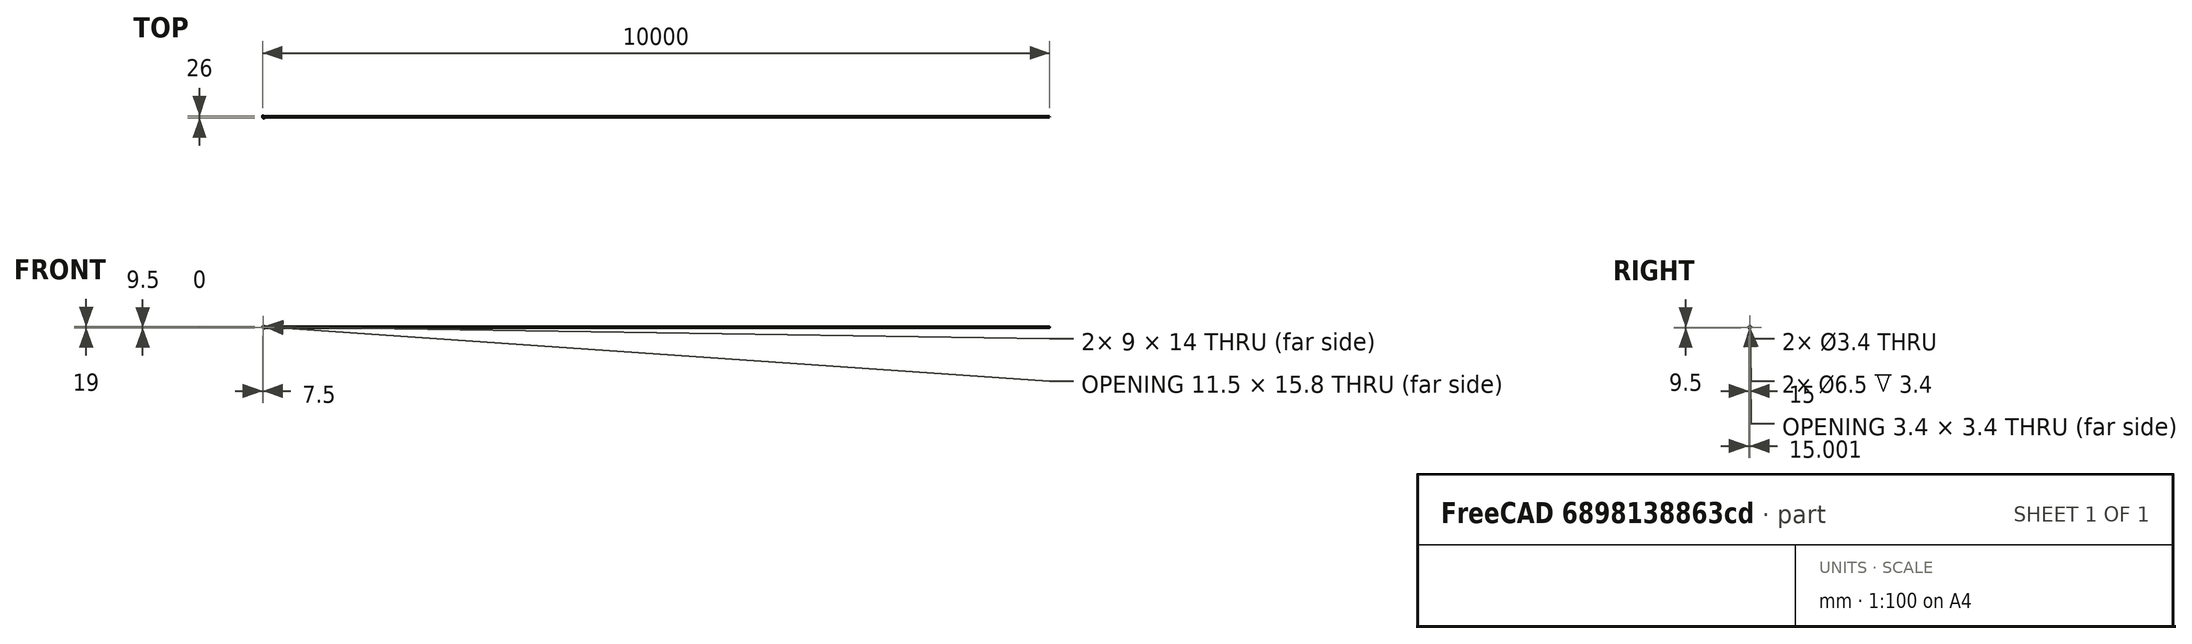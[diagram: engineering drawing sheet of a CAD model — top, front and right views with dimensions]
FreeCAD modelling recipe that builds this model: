
FCSTD DOCUMENT  (FreeCAD 0.14R3702 (Git))
Label: extruder-air-nozzle
License: CC-BY 3.0
LicenseURL: http://creativecommons.org/licenses/by/3.0/
objects: Part::Feature×7, Sketcher::SketchObject×7, PartDesign::Pad×4, PartDesign::Pocket×3, Part::MultiFuse×3, Part::Cylinder×2, Mesh::Feature×1, Part::Cut×1
note: 34 computed .brp shape members not serialized (recipe doc carries the construction recipe); baked Part::Feature solids carry a one-line shape summary decoded from their .brp

FEATURE [Mesh::Feature] Tobera_05
FEATURE [Part::Feature] Tobera_05001
  shape: bbox 25 x 26 x 19 mm, 3312 faces, 0 solids (baked)
FEATURE [Part::Feature] Tobera_05001_solid  label="Tobera_05001 (Solid)"
  shape: bbox 25 x 26 x 19 mm, 3312 faces (baked)
FEATURE [Part::Feature] Tobera_05001_solid001  label="Tobera_05001 (Solid)001"
  shape: bbox 25 x 26 x 19 mm, 2032 faces (baked)
FEATURE [Part::Feature] Tobera_05001_solid_cs
  shape: bbox 25 x 26 x 2e-07 mm, 0 faces, 0 solids (baked)
FEATURE [Sketcher::SketchObject] Sketch  label="main-body-sketch"
  sketch-geometry (10):
    g0: LineSegment StartX=0 StartY=0 StartZ=0 EndX=-15 EndY=0 EndZ=0
    g1: LineSegment StartX=-15 StartY=0 StartZ=0 EndX=-15 EndY=-8 EndZ=0
    g2: LineSegment StartX=-2 StartY=-21 StartZ=0 EndX=3.42 EndY=-21 EndZ=0
    g3: ArcOfCircle CenterX=-2 CenterY=-8 CenterZ=0 NormalX=0 NormalY=0 NormalZ=1 Radius=13 StartAngle=3.14159 EndAngle=4.71239
    g4: LineSegment StartX=0 StartY=0 StartZ=0 EndX=0 EndY=-10 EndZ=0
    g5: LineSegment StartX=1.99785 StartY=-13.4896 StartZ=0 EndX=9.99785 EndY=-18.6059 EndZ=0
    g6: LineSegment StartX=3.42 StartY=-21 StartZ=0 EndX=9.99785 EndY=-18.6059 EndZ=0
    g7: LineSegment [constr] StartX=3.42 StartY=-21 StartZ=0 EndX=9.42 EndY=-21 EndZ=0
    g8: LineSegment [constr] StartX=9.99785 StartY=-18.6059 StartZ=0 EndX=3.99785 EndY=-18.6059 EndZ=0
    g9: ArcOfCircle CenterX=4.04659 CenterY=-10 CenterZ=0 NormalX=0 NormalY=0 NormalZ=1 Radius=4.04659 StartAngle=3.14159 EndAngle=4.18151
  constraints (31):
    c: Coincident(g0,g1)
    c: Horizontal(g0)
    c: Vertical(g1)
    c: Horizontal(g2)
    c: Coincident(g0,g-1)
    c: DistanceX(g0) = -15
    c: DistanceY(g1) = -8
    c: DistanceX(g2) = 5.42
    c: DistanceY(g-1,g2) = -21
    c: Coincident(g3,g2)
    c: Coincident(g3,g1)
    c: Tangent(g1,g3)
    c: Tangent(g2,g3)
    c: Coincident(g4,g-1)
    c: Vertical(g4)
    c: DistanceY(g4) = -10
    c: Coincident(g6,g2)
    c: Distance(g6) = 7
    c: Horizontal(g7)
    c: Coincident(g7,g2)
    c: DistanceX(g7) = 6
    c: Angle(g7,g6) = 0.349066
    c: Coincident(g5,g6)
    c: Horizontal(g8)
    c: Coincident(g8,g5)
    c: Angle(g5,g8) = 0.568977
    c: DistanceX(g8) = -6
    c: DistanceX(g5,g5) = -8
    c: Coincident(g9,g4)
    c: Coincident(g9,g5)
    c: Tangent(g4,g9)
FEATURE [PartDesign::Pad] Pad  label="main-body"
  Length = 19
  Length2 = 100
  Midplane = true
  Sketch = -> Sketch
  Type = 0
FEATURE [Sketcher::SketchObject] Sketch001  label="Inner-room-sketch"
  sketch-geometry (18):
    g0: LineSegment [constr] StartX=-12 StartY=0 StartZ=0 EndX=-3 EndY=0 EndZ=0
    g1: LineSegment StartX=-12 StartY=0 StartZ=0 EndX=-12 EndY=-7.3 EndZ=0
    g2: LineSegment StartX=-5.40703 StartY=-16.2671 StartZ=0 EndX=6.32941 EndY=-19.9338 EndZ=0
    g3: LineSegment StartX=-3 StartY=0 StartZ=0 EndX=-3 EndY=-6 EndZ=0
    g4: ArcOfCircle CenterX=7 CenterY=-6.00002 CenterZ=0 NormalX=0 NormalY=0 NormalZ=1 Radius=10 StartAngle=3.14159 EndAngle=4.14341
    g5: LineSegment StartX=1.61229 StartY=-14.4245 StartZ=0 EndX=8.81324 EndY=-19.0297 EndZ=0
    g6: LineSegment [constr] StartX=6.32941 StartY=-19.9338 StartZ=0 EndX=8.81324 EndY=-19.0297 EndZ=0
    g7: LineSegment [constr] StartX=6.32941 StartY=-19.9338 StartZ=0 EndX=0.329406 EndY=-19.9338 EndZ=0
    g8: LineSegment [constr] StartX=6.32941 StartY=-19.9338 StartZ=0 EndX=9.32941 EndY=-19.9338 EndZ=0
    g9: GeomPoint [constr] X=3.4 Y=-21 Z=0
    g10: LineSegment [constr] StartX=8.81324 StartY=-19.0297 StartZ=0 EndX=6.81324 EndY=-19.0297 EndZ=0
    g11: ArcOfCircle CenterX=-2.60553 CenterY=-7.30002 CenterZ=0 NormalX=0 NormalY=0 NormalZ=1 Radius=9.39447 StartAngle=3.14159 EndAngle=4.40957
    g12: LineSegment StartX=6.32941 StartY=-19.9338 StartZ=0 EndX=7.57927 EndY=-20.3243 EndZ=0
    g13: LineSegment StartX=7.57927 StartY=-20.3243 StartZ=0 EndX=9.65569 EndY=-19.5685 EndZ=0
    g14: LineSegment StartX=9.65569 StartY=-19.5685 StartZ=0 EndX=8.81324 EndY=-19.0297 EndZ=0
    g15: LineSegment StartX=-12 StartY=0 StartZ=0 EndX=-12 EndY=1 EndZ=0
    g16: LineSegment StartX=-12 StartY=1 StartZ=0 EndX=-3 EndY=1 EndZ=0
    g17: LineSegment StartX=-3 StartY=1 StartZ=0 EndX=-3 EndY=0 EndZ=0
  constraints (53):
    c: Horizontal(g0)
    c: PointOnObject(g0,g-1)
    c: DistanceX(g0) = 9
    c: DistanceX(g-1,g0) = -3
    c: Vertical(g1)
    c: Coincident(g1,g0)
    c: Coincident(g3,g0)
    c: Vertical(g3)
    c: DistanceY(g3) = -6
    c: Coincident(g4,g3)
    c: Tangent(g3,g4)
    c: Coincident(g6,g2)
    c: Horizontal(g7)
    c: Coincident(g7,g2)
    c: DistanceX(g7) = -6
    c: Angle(g2,g7) = 0.302815
    c: Horizontal(g8)
    c: Coincident(g8,g2)
    c: DistanceX(g8) = 3
    c: Angle(g8,g6) = 0.349066
    c: DistanceY(g-1,g9) = -21
    c: PointOnObject(g9,g6)
    c: Coincident(g5,g6)
    c: Horizontal(g10)
    c: Coincident(g10,g5)
    c: DistanceX(g10) = -2
    c: Angle(g5,g10) = 0.568977
    c: Coincident(g5,g4)
    c: DistanceX(g-1,g9) = 3.4
    c: Tangent(g4,g5)
    c: Radius(g4) = 10
    c: Coincident(g11,g1)
    c: Coincident(g11,g2)
    c: Tangent(g2,g11)
    c: Tangent(g1,g11)
    c: Radius(g11) = 9.39447
    c: DistanceY(g1) = -7.3
    c: Coincident(g12,g13)
    c: Coincident(g13,g14)
    c: Coincident(g14,g5)
    c: PointOnObject(g13,g5)
    c: Coincident(g12,g2)
    c: PointOnObject(g12,g2)
    c: Parallel(g6,g13)
    c: Distance(g14) = 1
    c: Coincident(g15,g16)
    c: Coincident(g16,g17)
    c: Horizontal(g16)
    c: Vertical(g15)
    c: Vertical(g17)
    c: Coincident(g15,g0)
    c: Coincident(g17,g0)
    c: DistanceY(g15) = 1
FEATURE [PartDesign::Pad] Pad001  label="Inner-room"
  Length = 17
  Length2 = 100
  Midplane = true
  Sketch = -> Sketch001
  Type = 0
FEATURE [Sketcher::SketchObject] Sketch002  label="inner-cutout-1-sketch"
  ExternalGeometry = -> [Pad001]
  Placement = pos=(-3,-4e-12,0) rot=(0.57735,0.57735,0.57735;2.0944rad)
  Support = -> Pad001 [Face10]
  sketch-geometry (8):
    g0: LineSegment StartX=-5 StartY=8.5 StartZ=0 EndX=1 EndY=8.5 EndZ=0
    g1: LineSegment StartX=1 StartY=8.5 StartZ=0 EndX=1 EndY=7 EndZ=0
    g2: LineSegment StartX=1 StartY=7 StartZ=0 EndX=-5 EndY=7 EndZ=0
    g3: LineSegment StartX=-5 StartY=7 StartZ=0 EndX=-5 EndY=8.5 EndZ=0
    g4: LineSegment StartX=-5 StartY=-7 StartZ=0 EndX=1 EndY=-7 EndZ=0
    g5: LineSegment StartX=1 StartY=-7 StartZ=0 EndX=1 EndY=-8.5 EndZ=0
    g6: LineSegment StartX=1 StartY=-8.5 StartZ=0 EndX=-5 EndY=-8.5 EndZ=0
    g7: LineSegment StartX=-5 StartY=-8.5 StartZ=0 EndX=-5 EndY=-7 EndZ=0
  constraints (23):
    c: Coincident(g0,g1)
    c: Coincident(g1,g2)
    c: Coincident(g2,g3)
    c: Coincident(g3,g0)
    c: Horizontal(g0)
    c: Horizontal(g2)
    c: Vertical(g1)
    c: Vertical(g3)
    c: PointOnObject(g0,g-3)
    c: DistanceY(g3) = 1.5
    c: PointOnObject(g1,g-4)
    c: DistanceX(g2) = -6
    c: Coincident(g4,g5)
    c: Coincident(g5,g6)
    c: Coincident(g6,g7)
    c: Coincident(g7,g4)
    c: Horizontal(g4)
    c: Horizontal(g6)
    c: Vertical(g5)
    c: Vertical(g7)
    c: Symmetric(g5,g0,g-1)
    c: Symmetric(g4,g1,g-1)
    c: Symmetric(g4,g2,g-1)
FEATURE [PartDesign::Pocket] Pocket  label="inner-cutout-1"
  Length = 5
  Sketch = -> Sketch002
  Type = 1
FEATURE [Part::Cut] Cut  label="body-1"
  Base = -> Pad
  Tool = -> Pocket
FEATURE [Part::Cylinder] Cylinder  label="screw-tube-1"
  Angle = 360
  Height = 11
  Placement = pos=(-12.6,-6,0) rot=(0,1,0;1.5708rad)
  Radius = 2.7
FEATURE [Part::Cylinder] Cylinder001  label="screw-tube-2"
  Angle = 360
  Height = 3.4
  Placement = pos=(-13,-6,0) rot=(0,1,0;1.5708rad)
  Radius = 4.25
FEATURE [Part::MultiFuse] Fusion  label="screw-tube"
  Shapes = -> [Cylinder,Cylinder001]
FEATURE [Part::MultiFuse] Fusion001  label="body-2"
  Shapes = -> [Cut,Fusion]
FEATURE [Sketcher::SketchObject] Sketch003  label="bolt-cap-cutout-sketch-1"
  Placement = pos=(-15,0,0) rot=(0.57735,-0.57735,-0.57735;2.0944rad)
  Support = -> Fusion001 [Face5]
  sketch-geometry (1):
    g0: Circle CenterX=6 CenterY=0 CenterZ=0 NormalX=0 NormalY=0 NormalZ=1 Radius=3.25
  constraints (3):
    c: Radius(g0) = 3.25
    c: PointOnObject(g0,g-1)
    c: DistanceX(g-1,g0) = 6
FEATURE [PartDesign::Pocket] Pocket001  label="bolt-cap-cutout-sketch-002"
  Length = 3.4
  Sketch = -> Sketch003
  Type = 0
FEATURE [Sketcher::SketchObject] Sketch004  label="drill-sketch"
  Placement = pos=(-15,0,0) rot=(0.57735,-0.57735,-0.57735;2.0944rad)
  Support = -> Pocket001 [Face5]
  sketch-geometry (1):
    g0: Circle CenterX=6 CenterY=0 CenterZ=0 NormalX=0 NormalY=0 NormalZ=1 Radius=1.7
  constraints (3):
    c: Radius(g0) = 1.7
    c: PointOnObject(g0,g-1)
    c: DistanceX(g-1,g0) = 6
FEATURE [PartDesign::Pocket] Pocket002  label="drill"
  Length = 5
  Sketch = -> Sketch004
  Type = 1
FEATURE [Sketcher::SketchObject] Sketch005  label="top-sketch"
  ExternalGeometry = -> [Pocket002]
  Placement = pos=(0,0,0) rot=(0,0.707107,0.707107;3.14159rad)
  Support = -> Pocket002 [Face1]
  sketch-geometry (15):
    g0: LineSegment StartX=3 StartY=7 StartZ=0 EndX=12 EndY=7 EndZ=0
    g1: LineSegment StartX=12 StartY=7 StartZ=0 EndX=12 EndY=-7 EndZ=0
    g2: LineSegment StartX=12 StartY=-7 StartZ=0 EndX=3 EndY=-7 EndZ=0
    g3: LineSegment StartX=3 StartY=-7 StartZ=0 EndX=3 EndY=7 EndZ=0
    g4: ArcOfCircle CenterX=3.25 CenterY=6.4 CenterZ=0 NormalX=0 NormalY=0 NormalZ=1 Radius=1.5 StartAngle=1.5708 EndAngle=3.14159
    g5: LineSegment [constr] StartX=1.75 StartY=6.4 StartZ=0 EndX=3.25 EndY=6.4 EndZ=0
    g6: LineSegment [constr] StartX=3.25 StartY=7.9 StartZ=0 EndX=3.25 EndY=6.4 EndZ=0
    g7: LineSegment [constr] StartX=7.5 StartY=7 StartZ=0 EndX=7.5 EndY=-7 EndZ=0
    g8: LineSegment StartX=3.25 StartY=7.9 StartZ=0 EndX=11.75 EndY=7.9 EndZ=0
    g9: LineSegment StartX=3.25 StartY=-7.9 StartZ=0 EndX=11.75 EndY=-7.9 EndZ=0
    g10: LineSegment StartX=1.75 StartY=6.4 StartZ=0 EndX=1.75 EndY=-6.4 EndZ=0
    g11: LineSegment StartX=13.25 StartY=6.4 StartZ=0 EndX=13.25 EndY=-6.4 EndZ=0
    g12: ArcOfCircle CenterX=11.75 CenterY=6.4 CenterZ=0 NormalX=0 NormalY=0 NormalZ=1 Radius=1.5 StartAngle=0 EndAngle=1.5708
    g13: ArcOfCircle CenterX=11.75 CenterY=-6.4 CenterZ=0 NormalX=0 NormalY=0 NormalZ=1 Radius=1.5 StartAngle=4.71239 EndAngle=6.28319
    g14: ArcOfCircle CenterX=3.25 CenterY=-6.4 CenterZ=0 NormalX=0 NormalY=0 NormalZ=1 Radius=1.5 StartAngle=3.14159 EndAngle=4.71239
  constraints (42):
    c: Coincident(g0,g1)
    c: Coincident(g1,g2)
    c: Coincident(g2,g3)
    c: Coincident(g3,g0)
    c: Horizontal(g2)
    c: Vertical(g1)
    c: Vertical(g3)
    c: Coincident(g0,g-3)
    c: Coincident(g-3,g0)
    c: Symmetric(g0,g2,g-1)
    c: Horizontal(g5)
    c: Coincident(g5,g4)
    c: Coincident(g4,g5)
    c: Radius(g4) = 1.5
    c: Vertical(g6)
    c: Coincident(g6,g4)
    c: Coincident(g4,g6)
    c: DistanceX(g4,g0) = 1.25
    c: DistanceY(g0,g4) = 0.9
    c: Symmetric(g7,g7,g-1)
    c: PointOnObject(g7,g0)
    c: Symmetric(g0,g0,g7)
    c: Horizontal(g8)
    c: Coincident(g8,g4)
    c: Symmetric(g4,g8,g7)
    c: Horizontal(g9)
    c: Symmetric(g4,g9,g-1)
    c: Symmetric(g9,g9,g7)
    c: Symmetric(g10,g10,g-1)
    c: Coincident(g10,g4)
    c: Vertical(g11)
    c: Symmetric(g11,g11,g-1)
    c: Symmetric(g11,g4,g7)
    c: Coincident(g12,g8)
    c: Coincident(g12,g11)
    c: Equal(g12,g4)
    c: Coincident(g13,g11)
    c: Coincident(g13,g9)
    c: Equal(g13,g12)
    c: Coincident(g14,g9)
    c: Coincident(g14,g10)
    c: Equal(g14,g13)
FEATURE [PartDesign::Pad] Pad002  label="top"
  Length = 5
  Length2 = 100
  Sketch = -> Sketch005
  Type = 0
FEATURE [Sketcher::SketchObject] Sketch006  label="support-sketch"
  Placement = pos=(-3,0,0) rot=(0.57735,0.57735,0.57735;2.0944rad)
  sketch-geometry (4):
    g0: LineSegment StartX=4.6 StartY=-7.9 StartZ=0 EndX=5 EndY=-7.9 EndZ=0
    g1: LineSegment StartX=3 StartY=-9.5 StartZ=0 EndX=5 EndY=-9.5 EndZ=0
    g2: LineSegment StartX=5 StartY=-7.9 StartZ=0 EndX=5 EndY=-9.5 EndZ=0
    g3: LineSegment StartX=3 StartY=-9.5 StartZ=0 EndX=4.6 EndY=-7.9 EndZ=0
  constraints (12):
    c: Horizontal(g0)
    c: DistanceX(g-1,g0) = 5
    c: DistanceY(g-1,g0) = -7.9
    c: DistanceX(g0) = 0.4
    c: DistanceX(g1) = 2
    c: Vertical(g2)
    c: Horizontal(g1)
    c: DistanceY(g2) = -1.6
    c: Coincident(g2,g0)
    c: Coincident(g2,g1)
    c: Coincident(g3,g0)
    c: Coincident(g3,g1)
FEATURE [PartDesign::Pad] Pad003  label="support"
  Length = 9
  Length2 = 100
  Placement = pos=(-3,0,0) rot=(0.57735,0.57735,0.57735;2.0944rad)
  Reversed = true
  Sketch = -> Sketch006
  Type = 0
FEATURE [Part::Feature] Pad003001  label="support-final"
  Placement = pos=(-3,0,0) rot=(0.57735,0.57735,0.57735;2.0944rad)
  shape: bbox 9 x 2 x 1.6 mm, 6 faces (baked)
FEATURE [Part::Feature] Pad003002  label="air-nozzle-no-support"
  shape: bbox 25 x 26 x 19 mm, 37 faces (baked)
FEATURE [Part::Feature] Pad003002001  label="air-nozzle-final001"
  shape: bbox 25 x 26 x 19 mm, 37 faces (baked)
FEATURE [Part::MultiFuse] Fusion002  label="air-nozzle-with-support"
  Shapes = -> [Pad003001,Pad003002001]
